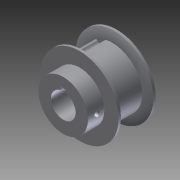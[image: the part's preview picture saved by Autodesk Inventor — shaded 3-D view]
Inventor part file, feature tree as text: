
AUTODESK INVENTOR PART (.ipt)
format: ipt  version: 2012 (Build 160160000, 160)  size: 198,144 bytes
history: native  units: in
note: dims shown in document units (in); Inventor stores cm internally (conversion verified against a paired STEP export)
features: extrude x1, imported_body x1, sketch x1
ambient origin geometry x8: Origin, YZ Plane, XZ Plane, XY Plane, X Axis, Y Axis, Z Axis, Center Point
feature tree (3):
  extrude  "Extrusion1"  Depth=0.0787in
  imported_body  "Base1"
  sketch  "Sketch2"  dims[d1=0.0787in d2=0.0787in d3=0.0394in d4=0.3157in d5=0.2269in d6=0.3937in d7=0.0in d8=0.375in]
